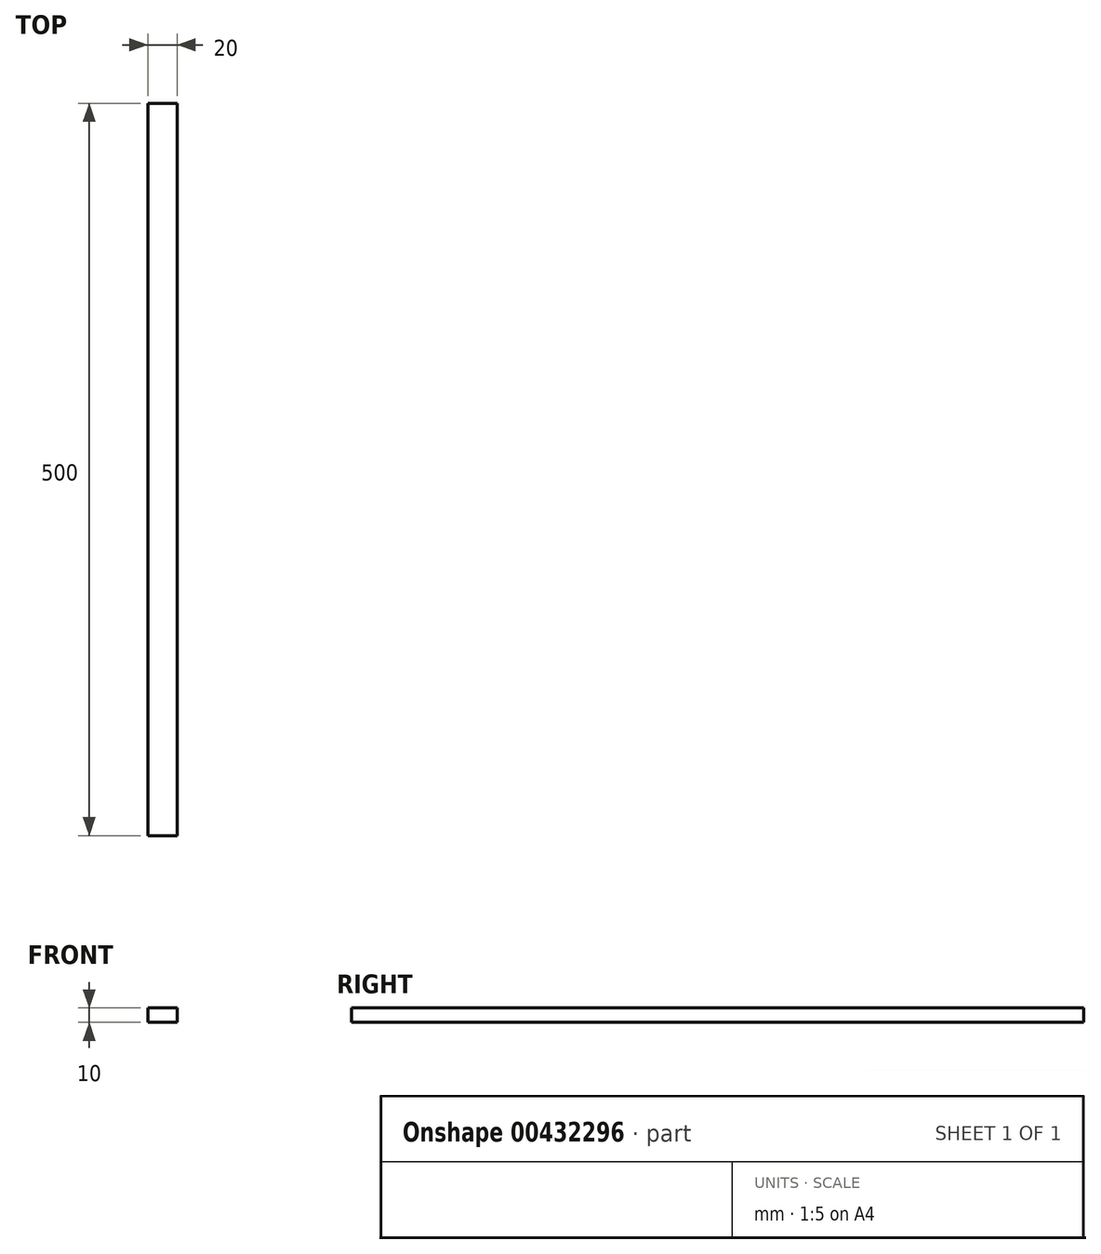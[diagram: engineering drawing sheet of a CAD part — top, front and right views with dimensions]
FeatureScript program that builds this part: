
annotation { "Feature Type Name" : "Feature", "Feature Type Description" : "" }
export const myFeature = defineFeature(function(context is Context, id is Id, definition is map)
    precondition{}
    {
        {
            var Q0;
            Q0=qCreatedBy(makeId("Top.planeOp"),FACE);
            var sketch = newSketch(context, id + "F0", { "sketchPlane" : qUnion([Q0])});
            skLineSegment(sketch, "E0.bottom", {"start": v(10, -250) * mm, "end": v(-10, -250) * mm});
            skLineSegment(sketch, "E0.top", {"start": v(10, 250) * mm, "end": v(-10, 250) * mm});
            skLineSegment(sketch, "E0.left", {"start": v(10, -250) * mm, "end": v(10, 250) * mm});
            skLineSegment(sketch, "E0.right", {"start": v(-10, -250) * mm, "end": v(-10, 250) * mm});
            skPoint(sketch, "E0.middle", {"position": v(0, 0) * mm});
            skSolve(sketch);
        }
        {
            var Q0;
            Q0=makeQuery(id+"F0.imprint","IMPRINT",FACE,{"disambiguationData":[TD([[makeQuery(id+"F0.imprint","IMPRINT",EDGE,{"derivedFrom":sQuery(id+"F0.wireOp",EDGE,"E0.bottom")}),-1.0]])]});
            extrude(context, id + "F1", {"entities" : qUnion([Q0]), "depth" : 10 * mm});
        }
    });
